# Revit family: Metal_Vented_Lockers-Salsbury_Industries-81000_Series-1_Wide_Units
name_source: partatom
category: Specialty Equipment
revit_build: Autodesk Revit 2016 (Build: 20150714_1515(x64)
units: mm (PartAtom-declared; Revit-internal decimal feet)

## family parameters
Always vertical = Yes
Cut with Voids When Loaded = No
OmniClass Number = 23.40.00.00
OmniClass Title = Equipment and Furnishings
Part Type = Normal
Room Calculation Point = No
Round Connector Dimension = Use Diameter
Shared = No
Work Plane-Based = No

## types (6) — shared parameters
Assembly Code = C1030310
Door Location D1 = Vented Metal Locker Doors-15 inch with Hasps : Single Tier Door - 6 foot
Hasp Handle Material = Plastic - Salsbury Finish - Black
Hasp Plate Rivet Material = Steel -Salsbury Finish - Polished Steel
Manufacturer = Salsbury Industries
MasterFormat Number = 10 51 13
MasterFormat Title = Lockers
OmniClass 23 Number = 23.40.00.00
OmniClass 23 Title = Equipment and Furnishings
Type Comments = 15" Wide Vented Metal Locker - Single Tier
URL = www.lockers.com
Unit Height = 72 "
Vent Array Spacing = 1.187 "
Vent Configuration Height = Vents : 6 foot high vents
Version = 2.0 (02/28/18)
Width = 15.04 "

## per-type parameters (varying)
| type | Base Height | Depth | Description | Model | Sloping Hood Height | Standard Leg Base | Vent Array 1 | Vent Array 2 | Vent Offset | Zee Base |
| 81165 - with Standard 6" High Legs | 6 " | 15.01 " | 1 Wide - 6 Feet High - 15 Inches Deep | 81165 | 8.682 " | Metal Locker Legs : 6" High - 15"W x 15"D | 8 | 7 | 3.5 " | Metal Locker Zee Base : None |
| 81168 - with Standard 6" High Legs | 6 " | 18.01 " | 1 Wide - 6 Feet High - 18 Inches Deep | 81168 | 10.739 " | Metal Locker Legs : 6" High - 15"W x 18"D | 10 | 9 | 3.75 " | Metal Locker Zee Base : None |
| 81165 - with 77575 Zee Base and 77550 Lockers without Legs | 4 " | 15.01 " | 1 Wide - 6 Feet High - 15 Inches Deep with Zee Base and Lockers without Legs | 81165 with 77575 and 77550 | 8.682 " | Metal Locker Legs : No Legs | 8 | 7 | 3.5 " | Metal Locker Zee Base : 77575 - 15"W x 15"D |
| 81168 - with 77578 Zee Base and 77550 Lockers without Legs | 4 " | 18.01 " | 1 Wide - 6 Feet High - 18 Inches Deep with Zee Base and Lockers without Legs | 81168 with 77578 and 77550 | 10.739 " | Metal Locker Legs : No Legs | 10 | 9 | 3.75 " | Metal Locker Zee Base : 77578 - 15"W x 18"D |
| 81165 - with 77550 Lockers without Legs | 0 " | 15.01 " | 1 Wide - 6 Feet High - 15 Inches Deep with Lockers without Legs | 81165 with 77550 | 8.682 " | Metal Locker Legs : No Legs | 8 | 7 | 3.5 " | Metal Locker Zee Base : None |
| 81168 - with 77550 Lockers without Legs | 0 " | 18.01 " | 1 Wide - 6 Feet High - 18 Inches Deep with Lockers without Legs | 81168 with 77550 | 10.739 " | Metal Locker Legs : No Legs | 10 | 9 | 3.75 " | Metal Locker Zee Base : None |

## geometry (parser evidence)
native form markers: Sweep x67
no freeform markers — native parametric forms only
